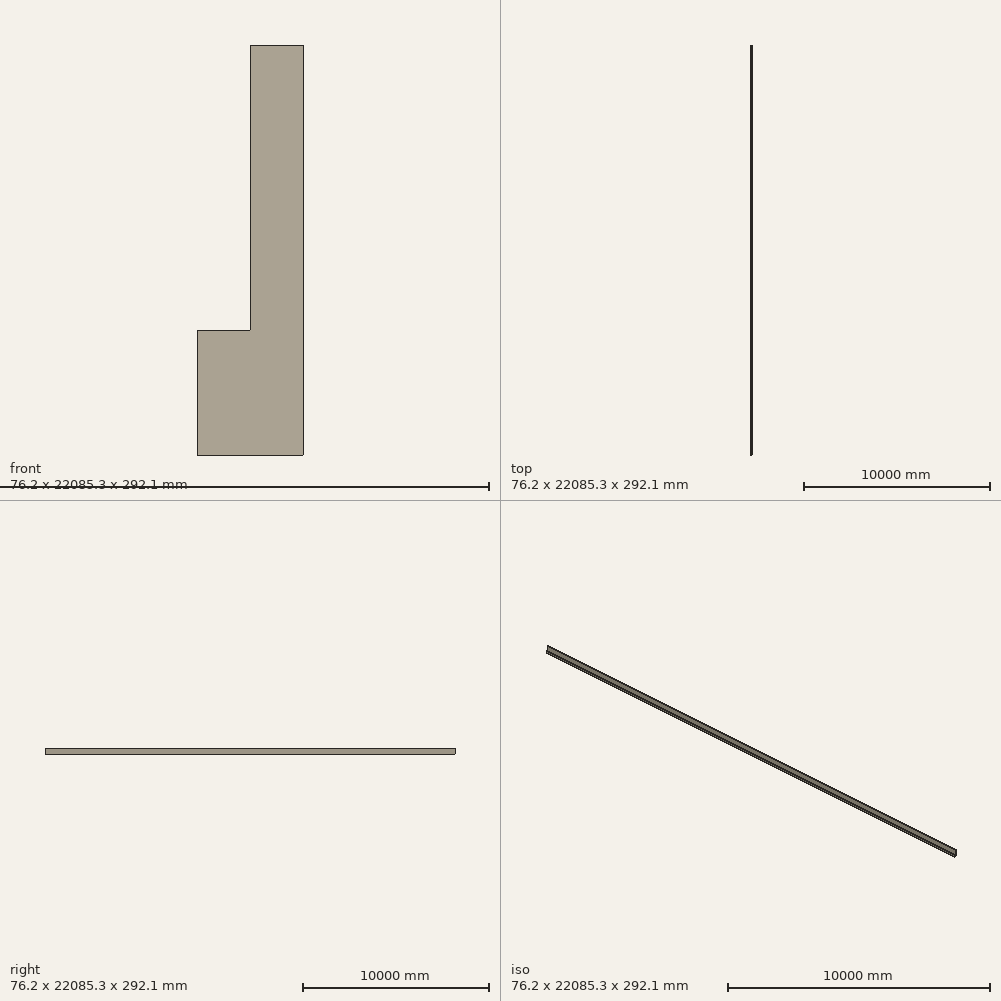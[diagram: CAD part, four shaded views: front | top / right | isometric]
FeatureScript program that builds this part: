
annotation { "Feature Type Name" : "Feature", "Feature Type Description" : "" }
export const myFeature = defineFeature(function(context is Context, id is Id, definition is map)
    precondition{}
    {
        {
            var Q0;
            Q0=qCreatedBy(makeId("Front.planeOp"),FACE);
            var sketch = newSketch(context, id + "F0", { "sketchPlane" : qUnion([Q0])});
            skLineSegment(sketch, "E0.bottom", {"start": v(0, 0) * mm, "end": v(76.2, 0) * mm});
            skLineSegment(sketch, "E0.top", {"start": v(0, 88.9) * mm, "end": v(38.1, 88.9) * mm});
            skLineSegment(sketch, "E0.left", {"start": v(0, 0) * mm, "end": v(0, 88.9) * mm});
            skLineSegment(sketch, "E1", {"start": v(76.2, 0) * mm, "end": v(76.2, 292.1) * mm});
            skLineSegment(sketch, "E2", {"start": v(76.2, 292.1) * mm, "end": v(38.1, 292.1) * mm});
            skLineSegment(sketch, "E3", {"start": v(38.1, 292.1) * mm, "end": v(38.1, 88.9) * mm});
            skSolve(sketch);
        }
        {
            var Q0;
            Q0 = qSketchRegion(id + "F0", true);
            extrude(context, id + "F1", {"entities" : qUnion([Q0]), "depth" : 22085.3 * mm, "offsetDistance" : 25.4 * mm});
        }
    });
